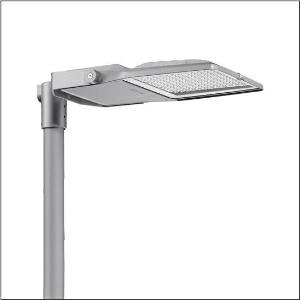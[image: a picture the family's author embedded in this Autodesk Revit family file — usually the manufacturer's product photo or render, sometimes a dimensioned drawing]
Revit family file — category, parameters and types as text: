
# Revit family: floodlight_fl_21_iq_midi___pl64_5xa7782f2e3a_4586
name_source: partatom
category: Lighting Fixtures
units: mm (PartAtom-declared; Revit-internal decimal feet)

## family parameters
Cut with Voids When Loaded = No
Host = Face
Light Source = No
Part Type = Normal
Room Calculation Point = No
Round Connector Dimension = Use Diameter
Shared = No

## types (1)
- --- (1 x LED, 34530 lm, 270.2 W, 3000K)
    Apparent Load = 270 VA
    CIE Flux Codes = 28 80 98 100 100
    Color Rendering = 70
    Color Temperature = 3000K
    Default Elevation = 1800 mm
    Description = Floodlight FL 21 iQ midi, floodlight, primary light control with lens, of PMMA, primary optical cover: protective disc, of toughened safety glass, transparent, light distribution: PL64, light emission: direct distribution, installation type: surface-mounted, lamps: LED, High Power LED, rated values: 34.530lm | 270,2W | 127,8lm/W (begin service life); end service life: 34.530lm | 286,6W; at 50% lumin. flux: 17.265lm | 117,4W | 147,1lm/W, colour temperature: 3000K, colour rendering: CRI > 70, light colour: 730, light setting 1 begin service life: 100% | 34.530lm | 270,2W | 127,8lm/W | 3.000K, light setting 1 end service life: 286,6W, further light settings possible, control: optimised constant luminous flux control (CLO 2.0), Desk-Remote (wireless, voltage-free reading and setting of iQ features in the workshop via application-optimized NFC function/RFID function), Smart-Wire, Night-Set, Temp-Guard, Auto-Match, Street-Remote, pre-setting: linear dimming characteristic, with terminal, 6-pole, mains connection: 220..240V, AC, 50/60Hz, luminaire housing, of diecast aluminium, powder-coated, SITECO metallic grey (DB 702S), corrosivity category C5 mid according to DIN EN ISO 12944suitable for swimming poolschlorine-resistant, sealing non-destructively replaceable, please order mast flange separately, mast bracket, of steel, galvanised, powder-coated, SITECO metallic grey (DB 702S), protection rating (complete): IP66, insulation class (complete): insulation class II (safety insulation), certification: CE, ENEC, VDE, protection symbol: D, impact resistance: IK08, permissible operating ambient temperature: -40..+40°C, permissible operating ambient temperature for outdoor applications: -40..+50°C, standard: DIN EN 12944, LABS conformity tested according to VDMA 24364:2018-05, packaging unit: 1 piece

Light Distribution: PL64
    Height = 76 mm
    Lamp = 1 x LED
    Lamp Light Flux = 34530 lm
    Lamp Power = 270.2 W
    Lamp count = 1
    Length = 657 mm
    Luminous efficacy = 128 lm/W
    Manufacturer = Siteco
    ModVariant = No
    Model = 5XA7782F2E3A
    Mounting Place = Pole
    Mounting Type = Pole annexe
    Number of Poles = 1
    OnlyDefault = Yes
    Power Factor = 1
    Product Name = Floodlight FL 21 iQ midi | PL64
    Product group = floodlight | pylon annexe
    ProductGroupID = 6201
    Protection Class = Protection class II
    Protection Degree = IP 66
    RLX_Detail_Level = 1
    RLX_Emergency_Light_Flux = 0 lm
    RLX_Emergency_Type = 0
    RLX_Emergency_Type_DB = No
    RlxData = <blob elided: 153737 chars, md5=14fb6d9d>
    Socket = socket
    Standby Power = 0 W
    System Light Flux = 34530 lm
    System Power = 270 W
    Type Comments = factory setting: luminous flux: 100 % | dim-lin: 254 | 620 mA
    Type Image = l_1007123.jpg
    URL = http://relux.com
    VarID = @adj_108179
    Voltage = 0 V
    Weight = 0.00 kg
    Width = 442 mm

## geometry (parser evidence)
native form markers: Blend x4, Sweep x14
no freeform markers — native parametric forms only
